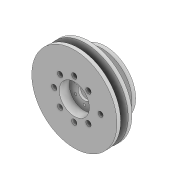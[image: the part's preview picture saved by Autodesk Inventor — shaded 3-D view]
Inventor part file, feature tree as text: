
AUTODESK INVENTOR PART (.ipt)
format: ipt  version: 2022 (Build 260153000, 153)  size: 377,344 bytes
history: native  units: mm
features: extrude x10, sketch x10, projected_geometry x5, thicken_offset x4, fillet x2, revolve x1, pattern_circular x1
ambient origin geometry x8: Origin, YZ Plane, XZ Plane, XY Plane, X Axis, Y Axis, Z Axis, Center Point
bodies: Solid1 (feature_tree)
feature tree (33):
  revolve  "Revolution1"  [1 undecoded]
  extrude  "Extrusion1"  Depth=1.5mm
  pattern_circular  "Circular Pattern1"  Count=10  [1 undecoded]
  extrude  "Extrusion2"  Depth=2.0mm
  extrude  "Extrusion3"  Depth=100.0mm TaperAngle=0.0deg
  extrude  "Extrusion8"  Depth=0.9mm TaperAngle=0.0deg
  extrude  "Extrusion6"  Depth=0.9mm
  extrude  "Extrusion7"  Depth=0.9mm TaperAngle=0.0deg
  sketch  "Sketch11"  dims[d16=10.5mm d17=100.0mm d18=0.0mm]
  extrude  "Extrusion10"  Depth=0.9mm
  extrude  "Extrusion11"  Depth=0.9mm TaperAngle=0.0deg
  thicken_offset  "Thicken1"
  thicken_offset  "Thicken2"
  thicken_offset  "Thicken3"
  fillet  "Fillet1"  Radius=18.0mm
  thicken_offset  "Thicken4"
  fillet  "Fillet2"  Radius=1.5mm
  extrude  "Extrusion12"  Depth=0.9mm
  extrude  "Extrusion9"  Depth=1.0mm TaperAngle=0.0deg
  sketch  "Sketch1"  dims[d0=6.0mm d1=3.0mm]
  sketch  "Sketch2"  dims[d2=14.0mm d4=1.5mm]
  sketch  "Sketch3"  dims[d5=1.5mm]
  sketch  "Sketch4"  dims[d6=360.0deg]
  projected_geometry  "Projected Loop1"
  projected_geometry  "Projected Loop2"
  sketch  "Sketch7"  dims[d7=2.1mm]
  sketch  "Sketch8"  dims[d8=8.0mm]
  projected_geometry  "Projected Loop5"
  sketch  "Sketch9"  dims[d9=9.0mm d10=100.0mm d11=0.0mm]
  sketch  "Sketch10"  dims[d12=80.0mm d13=360.0deg d15=2.0mm]
  sketch  "Sketch12"  dims[d19=4.0mm d20=5.0mm d21=0.0mm d24=10.5mm d25=2.0mm d26=0.0mm d31=2.0mm d32=4.0mm d33=0.0mm d34=18.0mm d35=1.5mm d36=0.0mm d37=5.0mm d38=1.0mm d39=0.0mm d40=100.0mm d41=0.0mm d44=4.0mm d45=4.0mm d46=4.0mm d47=4.0mm d48=4.0mm d49=4.0mm d50=4.0mm d51=3.0mm d52=3.0mm d53=3.0mm d54=1.6mm d55=0.0mm d56=6.0mm d57=0.0mm d58=23.0mm d59=3.0mm d60=2.0mm d61=3.0mm d62=3.0mm d63=3.0mm d64=3.0mm d65=1.0mm d66=1.5mm d67=1.5mm d68=0.9mm d69=1.05mm d70=4.0mm d71=60.0mm d73=360.0deg d75=100.0mm d76=0.0mm d42=0.5mm d43=0.872665mm]
  projected_geometry  "Projected Loop6"
  projected_geometry  "Project Cut Edges1"
note: 2 required parameter values undecoded (feature->parameter linkage not recoverable at this tier; creation-order binding heuristic only, values carry confidence <= 0.55)